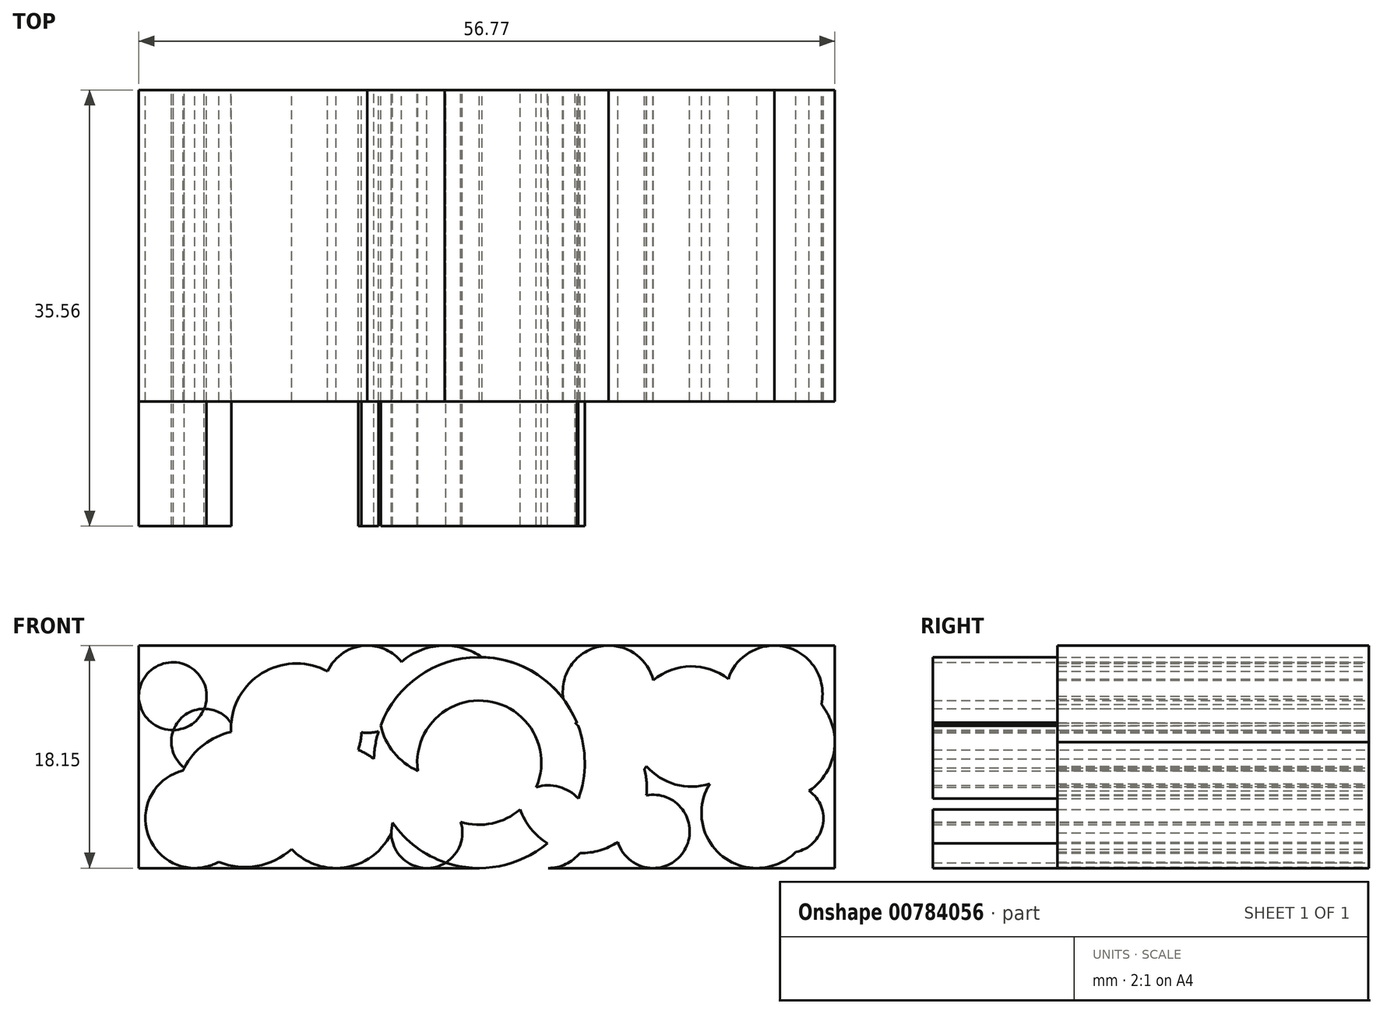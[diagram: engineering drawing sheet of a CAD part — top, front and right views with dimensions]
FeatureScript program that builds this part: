
annotation { "Feature Type Name" : "Feature", "Feature Type Description" : "" }
export const myFeature = defineFeature(function(context is Context, id is Id, definition is map)
    precondition{}
    {
        {
            var Q0;
            Q0=qCreatedBy(makeId("Front.planeOp"),FACE);
            var sketch = newSketch(context, id + "F0", { "sketchPlane" : qUnion([Q0])});
            skLineSegment(sketch, "E0.bottom", {"start": v(-27.77, 0) * mm, "end": v(29, 0) * mm});
            skLineSegment(sketch, "E0.top", {"start": v(-27.77, 18.15) * mm, "end": v(29, 18.15) * mm});
            skLineSegment(sketch, "E0.left", {"start": v(-27.77, 0) * mm, "end": v(-27.77, 18.15) * mm});
            skLineSegment(sketch, "E0.right", {"start": v(29, 0) * mm, "end": v(29, 18.15) * mm});
            skCircle(sketch, "E1", {"center": v(-19.1, 5.65) * mm, "radius": 5.57 * mm});
            skCircle(sketch, "E2", {"center": v(-11.7, 4.99) * mm, "radius": 4.99 * mm});
            skCircle(sketch, "E3", {"center": v(-14.93, 11.36) * mm, "radius": 5.33 * mm});
            skCircle(sketch, "E4", {"center": v(0, 8.6) * mm, "radius": 8.6 * mm});
            skCircle(sketch, "E5", {"center": v(5.61, 3.37) * mm, "radius": 3.37 * mm});
            skCircle(sketch, "E6", {"center": v(-4.28, 2.9) * mm, "radius": 2.9 * mm});
            skCircle(sketch, "E7", {"center": v(0, 8.6) * mm, "radius": 5.06 * mm});
            skCircle(sketch, "E8", {"center": v(10.56, 14.4) * mm, "radius": 3.75 * mm});
            skCircle(sketch, "E9", {"center": v(17.3, 11.55) * mm, "radius": 4.9 * mm});
            skCircle(sketch, "E10", {"center": v(10.75, 9.84) * mm, "radius": 3.25 * mm});
            skCircle(sketch, "E11", {"center": v(14.17, 3) * mm, "radius": 3 * mm});
            skCircle(sketch, "E12", {"center": v(8.35, 6.55) * mm, "radius": 5.32 * mm});
            skCircle(sketch, "E13", {"center": v(22.63, 4.51) * mm, "radius": 4.51 * mm});
            skCircle(sketch, "E14", {"center": v(-9.13, 14.6) * mm, "radius": 3.56 * mm});
            skCircle(sketch, "E15", {"center": v(-2.82, 12.8) * mm, "radius": 5.34 * mm});
            skCircle(sketch, "E16", {"center": v(-25, 14.02) * mm, "radius": 2.76 * mm});
            skCircle(sketch, "E17", {"center": v(-22.44, 10.31) * mm, "radius": 2.68 * mm});
            skCircle(sketch, "E18", {"center": v(-23.2, 4.04) * mm, "radius": 4.04 * mm});
            skCircle(sketch, "E19", {"center": v(24.06, 14.21) * mm, "radius": 3.94 * mm});
            skCircle(sketch, "E20", {"center": v(24.17, 10.28) * mm, "radius": 4.83 * mm});
            skCircle(sketch, "E21", {"center": v(25.3, 4.04) * mm, "radius": 2.77 * mm});
            skSolve(sketch);
        }
        {
            var Q0;
            {var subQ1=sQuery(id+"F0.wireOp",EDGE,"E0.top");var subQ7=sQuery(id+"F0.wireOp",EDGE,"E0.left");var subQ8=makeQuery(id+"F0.imprint","INTERSECT",VERTEX,{"derivedFrom":[subQ1,subQ7]});Q0=makeQuery(id+"F0.imprint","IMPRINT",FACE,{"disambiguationData":[TD([[makeQuery(id+"F0.imprint","IMPRINT",EDGE,{"disambiguationData":[TD([[subQ8,-1.0]])],"derivedFrom":subQ1}),-1.0]])]});}
            var Q1;
            {var subQ0=sQuery(id+"F0.wireOp",EDGE,"E14");var subQ1=sQuery(id+"F0.wireOp",EDGE,"E0.top");var subQ2=makeQuery(id+"F0.imprint","INTERSECT",VERTEX,{"derivedFrom":[subQ1,subQ0]});Q1=makeQuery(id+"F0.imprint","IMPRINT",FACE,{"disambiguationData":[TD([[makeQuery(id+"F0.imprint","IMPRINT",EDGE,{"disambiguationData":[TD([[subQ2,-1.0]])],"derivedFrom":subQ1}),-1.0]])]});}
            var Q2;
            {var subQ0=sQuery(id+"F0.wireOp",EDGE,"E15");var subQ1=sQuery(id+"F0.wireOp",EDGE,"E0.top");var subQ2=makeQuery(id+"F0.imprint","INTERSECT",VERTEX,{"derivedFrom":[subQ1,subQ0]});Q2=makeQuery(id+"F0.imprint","IMPRINT",FACE,{"disambiguationData":[TD([[makeQuery(id+"F0.imprint","IMPRINT",EDGE,{"disambiguationData":[TD([[subQ2,-1.0]])],"derivedFrom":subQ1}),-1.0]])]});}
            var Q3;
            {var subQ0=sQuery(id+"F0.wireOp",EDGE,"E8");var subQ1=sQuery(id+"F0.wireOp",EDGE,"E0.top");var subQ2=makeQuery(id+"F0.imprint","INTERSECT",VERTEX,{"derivedFrom":[subQ1,subQ0]});Q3=makeQuery(id+"F0.imprint","IMPRINT",FACE,{"disambiguationData":[TD([[makeQuery(id+"F0.imprint","IMPRINT",EDGE,{"disambiguationData":[TD([[subQ2,-1.0]])],"derivedFrom":subQ1}),-1.0]])]});}
            var Q4;
            {var subQ0=sQuery(id+"F0.wireOp",EDGE,"E0.right");var subQ1=sQuery(id+"F0.wireOp",EDGE,"E0.top");var subQ2=makeQuery(id+"F0.imprint","INTERSECT",VERTEX,{"derivedFrom":[subQ1,subQ0]});Q4=makeQuery(id+"F0.imprint","IMPRINT",FACE,{"disambiguationData":[TD([[makeQuery(id+"F0.imprint","IMPRINT",EDGE,{"disambiguationData":[TD([[subQ2,1.0]])],"derivedFrom":subQ1}),-1.0]])]});}
            var Q5;
            {var subQ1=sQuery(id+"F0.wireOp",EDGE,"E0.right");var subQ6=sQuery(id+"F0.wireOp",EDGE,"E0.bottom");var subQ9=makeQuery(id+"F0.imprint","INTERSECT",VERTEX,{"derivedFrom":[subQ6,subQ1]});Q5=makeQuery(id+"F0.imprint","IMPRINT",FACE,{"disambiguationData":[TD([[makeQuery(id+"F0.imprint","IMPRINT",EDGE,{"disambiguationData":[TD([[subQ9,1.0]])],"derivedFrom":subQ6}),1.0]])]});}
            var Q6;
            {var subQ0=sQuery(id+"F0.wireOp",EDGE,"E11");var subQ1=sQuery(id+"F0.wireOp",EDGE,"E0.bottom");var subQ2=makeQuery(id+"F0.imprint","INTERSECT",VERTEX,{"derivedFrom":[subQ1,subQ0]});Q6=makeQuery(id+"F0.imprint","IMPRINT",FACE,{"disambiguationData":[TD([[makeQuery(id+"F0.imprint","IMPRINT",EDGE,{"disambiguationData":[TD([[subQ2,-1.0]])],"derivedFrom":subQ1}),1.0]])]});}
            var Q7;
            {var subQ0=sQuery(id+"F0.wireOp",EDGE,"E5");var subQ1=sQuery(id+"F0.wireOp",EDGE,"E0.bottom");var subQ2=makeQuery(id+"F0.imprint","INTERSECT",VERTEX,{"derivedFrom":[subQ1,subQ0]});Q7=makeQuery(id+"F0.imprint","IMPRINT",FACE,{"disambiguationData":[TD([[makeQuery(id+"F0.imprint","IMPRINT",EDGE,{"disambiguationData":[TD([[subQ2,-1.0]])],"derivedFrom":subQ1}),1.0]])]});}
            var Q8;
            {var subQ0=sQuery(id+"F0.wireOp",EDGE,"E2");var subQ1=sQuery(id+"F0.wireOp",EDGE,"E0.bottom");var subQ2=makeQuery(id+"F0.imprint","INTERSECT",VERTEX,{"derivedFrom":[subQ1,subQ0]});Q8=makeQuery(id+"F0.imprint","IMPRINT",FACE,{"disambiguationData":[TD([[makeQuery(id+"F0.imprint","IMPRINT",EDGE,{"disambiguationData":[TD([[subQ2,-1.0]])],"derivedFrom":subQ1}),1.0]])]});}
            var Q9;
            {var subQ0=sQuery(id+"F0.wireOp",EDGE,"E6");var subQ1=sQuery(id+"F0.wireOp",EDGE,"E0.bottom");var subQ2=makeQuery(id+"F0.imprint","INTERSECT",VERTEX,{"derivedFrom":[subQ1,subQ0]});Q9=makeQuery(id+"F0.imprint","IMPRINT",FACE,{"disambiguationData":[TD([[makeQuery(id+"F0.imprint","IMPRINT",EDGE,{"disambiguationData":[TD([[subQ2,-1.0]])],"derivedFrom":subQ1}),1.0]])]});}
            var Q10;
            {var subQ0=sQuery(id+"F0.wireOp",EDGE,"E18");var subQ1=sQuery(id+"F0.wireOp",EDGE,"E0.bottom");var subQ2=makeQuery(id+"F0.imprint","INTERSECT",VERTEX,{"derivedFrom":[subQ1,subQ0]});Q10=makeQuery(id+"F0.imprint","IMPRINT",FACE,{"disambiguationData":[TD([[makeQuery(id+"F0.imprint","IMPRINT",EDGE,{"disambiguationData":[TD([[subQ2,-1.0]])],"derivedFrom":subQ1}),1.0]])]});}
            var Q11;
            {var subQ1=sQuery(id+"F0.wireOp",EDGE,"E0.left");var subQ9=sQuery(id+"F0.wireOp",EDGE,"E0.bottom");var subQ10=makeQuery(id+"F0.imprint","INTERSECT",VERTEX,{"derivedFrom":[subQ9,subQ1]});Q11=makeQuery(id+"F0.imprint","IMPRINT",FACE,{"disambiguationData":[TD([[makeQuery(id+"F0.imprint","IMPRINT",EDGE,{"disambiguationData":[TD([[subQ10,-1.0]])],"derivedFrom":subQ9}),1.0]])]});}
            extrude(context, id + "F1", {"entities" : qUnion([Q0, Q1, Q2, Q3, Q4, Q5, Q6, Q7, Q8, Q9, Q10, Q11]), "depth" : 25.4 * mm, "offsetDistance" : 25.4 * mm});
        }
        {
            var Q0;
            {var subQ0=sQuery(id+"F0.wireOp",EDGE,"E16");var subQ1=makeQuery(id+"F0.imprint","INTERSECT",VERTEX,{"derivedFrom":[sQuery(id+"F0.wireOp",EDGE,"E0.left"),subQ0]});Q0=makeQuery(id+"F0.imprint","IMPRINT",FACE,{"disambiguationData":[TD([[makeQuery(id+"F0.imprint","IMPRINT",EDGE,{"disambiguationData":[TD([[subQ1,-1.0]])],"derivedFrom":subQ0}),1.0]])]});}
            var Q1;
            {var subQ1=sQuery(id+"F0.wireOp",EDGE,"E3");var subQ6=sQuery(id+"F0.wireOp",EDGE,"E1");var subQ7=makeQuery(id+"F0.imprint","INTERSECT",VERTEX,{"disambiguationData":[OD(1.0)],"derivedFrom":[subQ6,subQ1]});Q1=makeQuery(id+"F0.imprint","IMPRINT",FACE,{"disambiguationData":[TD([[makeQuery(id+"F0.imprint","IMPRINT",EDGE,{"disambiguationData":[TD([[subQ7,-1.0]])],"derivedFrom":subQ6}),-1.0]])]});}
            var Q2;
            {var subQ5=sQuery(id+"F0.wireOp",EDGE,"E2");var subQ7=sQuery(id+"F0.wireOp",EDGE,"E4");var subQ8=makeQuery(id+"F0.imprint","INTERSECT",VERTEX,{"disambiguationData":[OD(0.0)],"derivedFrom":[subQ5,subQ7]});Q2=makeQuery(id+"F0.imprint","IMPRINT",FACE,{"disambiguationData":[TD([[makeQuery(id+"F0.imprint","IMPRINT",EDGE,{"disambiguationData":[TD([[subQ8,1.0]])],"derivedFrom":subQ5}),-1.0]])]});}
            var Q3;
            {var subQ0=sQuery(id+"F0.wireOp",EDGE,"E15");var subQ1=sQuery(id+"F0.wireOp",EDGE,"E4");var subQ2=makeQuery(id+"F0.imprint","INTERSECT",VERTEX,{"disambiguationData":[OD(0.0)],"derivedFrom":[subQ1,subQ0]});Q3=makeQuery(id+"F0.imprint","IMPRINT",FACE,{"disambiguationData":[TD([[makeQuery(id+"F0.imprint","IMPRINT",EDGE,{"disambiguationData":[TD([[subQ2,-1.0]])],"derivedFrom":subQ1}),1.0]])]});}
            var Q4;
            {var subQ0=sQuery(id+"F0.wireOp",EDGE,"E14");var subQ1=sQuery(id+"F0.wireOp",EDGE,"E4");var subQ2=makeQuery(id+"F0.imprint","INTERSECT",VERTEX,{"disambiguationData":[OD(0.0)],"derivedFrom":[subQ1,subQ0]});Q4=makeQuery(id+"F0.imprint","IMPRINT",FACE,{"disambiguationData":[TD([[makeQuery(id+"F0.imprint","IMPRINT",EDGE,{"disambiguationData":[TD([[subQ2,-1.0]])],"derivedFrom":subQ1}),1.0]])]});}
            var Q5;
            {var subQ0=sQuery(id+"F0.wireOp",EDGE,"E4");var subQ1=sQuery(id+"F0.wireOp",EDGE,"E2");var subQ2=makeQuery(id+"F0.imprint","INTERSECT",VERTEX,{"disambiguationData":[OD(0.0)],"derivedFrom":[subQ1,subQ0]});Q5=makeQuery(id+"F0.imprint","IMPRINT",FACE,{"disambiguationData":[TD([[makeQuery(id+"F0.imprint","IMPRINT",EDGE,{"disambiguationData":[TD([[subQ2,1.0]])],"derivedFrom":subQ1}),1.0]])]});}
            var Q6;
            {var subQ1=sQuery(id+"F0.wireOp",EDGE,"E4");var subQ5=sQuery(id+"F0.wireOp",EDGE,"E2");var subQ8=makeQuery(id+"F0.imprint","INTERSECT",VERTEX,{"disambiguationData":[OD(1.0)],"derivedFrom":[subQ5,subQ1]});Q6=makeQuery(id+"F0.imprint","IMPRINT",FACE,{"disambiguationData":[TD([[makeQuery(id+"F0.imprint","IMPRINT",EDGE,{"disambiguationData":[TD([[subQ8,-1.0]])],"derivedFrom":subQ5}),-1.0]])]});}
            var Q7;
            {var subQ1=sQuery(id+"F0.wireOp",EDGE,"E4");var subQ8=makeQuery(id+"F0.imprint","INTERSECT",VERTEX,{"derivedFrom":[sQuery(id+"F0.wireOp",EDGE,"E0.bottom"),subQ1]});Q7=makeQuery(id+"F0.imprint","IMPRINT",FACE,{"disambiguationData":[TD([[makeQuery(id+"F0.imprint","IMPRINT",EDGE,{"disambiguationData":[TD([[subQ8,1.0]])],"derivedFrom":subQ1}),1.0]])]});}
            var Q8;
            {var subQ0=sQuery(id+"F0.wireOp",EDGE,"E5");var subQ1=sQuery(id+"F0.wireOp",EDGE,"E4");var subQ2=makeQuery(id+"F0.imprint","INTERSECT",VERTEX,{"disambiguationData":[OD(0.0)],"derivedFrom":[subQ1,subQ0]});Q8=makeQuery(id+"F0.imprint","IMPRINT",FACE,{"disambiguationData":[TD([[makeQuery(id+"F0.imprint","IMPRINT",EDGE,{"disambiguationData":[TD([[subQ2,-1.0]])],"derivedFrom":subQ1}),1.0]])]});}
            var Q9;
            {var subQ0=sQuery(id+"F0.wireOp",EDGE,"E12");var subQ1=sQuery(id+"F0.wireOp",EDGE,"E4");var subQ2=makeQuery(id+"F0.imprint","INTERSECT",VERTEX,{"disambiguationData":[OD(1.0)],"derivedFrom":[subQ1,subQ0]});Q9=makeQuery(id+"F0.imprint","IMPRINT",FACE,{"disambiguationData":[TD([[makeQuery(id+"F0.imprint","IMPRINT",EDGE,{"disambiguationData":[TD([[subQ2,-1.0]])],"derivedFrom":subQ1}),1.0]])]});}
            var Q10;
            {var subQ1=sQuery(id+"F0.wireOp",EDGE,"E5");var subQ9=sQuery(id+"F0.wireOp",EDGE,"E4");var subQ10=makeQuery(id+"F0.imprint","INTERSECT",VERTEX,{"disambiguationData":[OD(1.0)],"derivedFrom":[subQ9,subQ1]});Q10=makeQuery(id+"F0.imprint","IMPRINT",FACE,{"disambiguationData":[TD([[makeQuery(id+"F0.imprint","IMPRINT",EDGE,{"disambiguationData":[TD([[subQ10,-1.0]])],"derivedFrom":subQ9}),1.0]])]});}
            var Q11;
            {var subQ0=sQuery(id+"F0.wireOp",EDGE,"E8");var subQ1=sQuery(id+"F0.wireOp",EDGE,"E4");var subQ2=makeQuery(id+"F0.imprint","INTERSECT",VERTEX,{"disambiguationData":[OD(1.0)],"derivedFrom":[subQ1,subQ0]});Q11=makeQuery(id+"F0.imprint","IMPRINT",FACE,{"disambiguationData":[TD([[makeQuery(id+"F0.imprint","IMPRINT",EDGE,{"disambiguationData":[TD([[subQ2,-1.0]])],"derivedFrom":subQ1}),1.0]])]});}
            var Q12;
            {var subQ0=sQuery(id+"F0.wireOp",EDGE,"E8");var subQ1=sQuery(id+"F0.wireOp",EDGE,"E4");var subQ2=makeQuery(id+"F0.imprint","INTERSECT",VERTEX,{"disambiguationData":[OD(0.0)],"derivedFrom":[subQ1,subQ0]});Q12=makeQuery(id+"F0.imprint","IMPRINT",FACE,{"disambiguationData":[TD([[makeQuery(id+"F0.imprint","IMPRINT",EDGE,{"disambiguationData":[TD([[subQ2,1.0]])],"derivedFrom":subQ1}),1.0]])]});}
            extrude(context, id + "F2", {"entities" : qUnion([Q0, Q1, Q2, Q3, Q4, Q5, Q6, Q7, Q8, Q9, Q10, Q11, Q12]), "depth" : 35.56 * mm, "offsetDistance" : 25.4 * mm});
        }
    });
